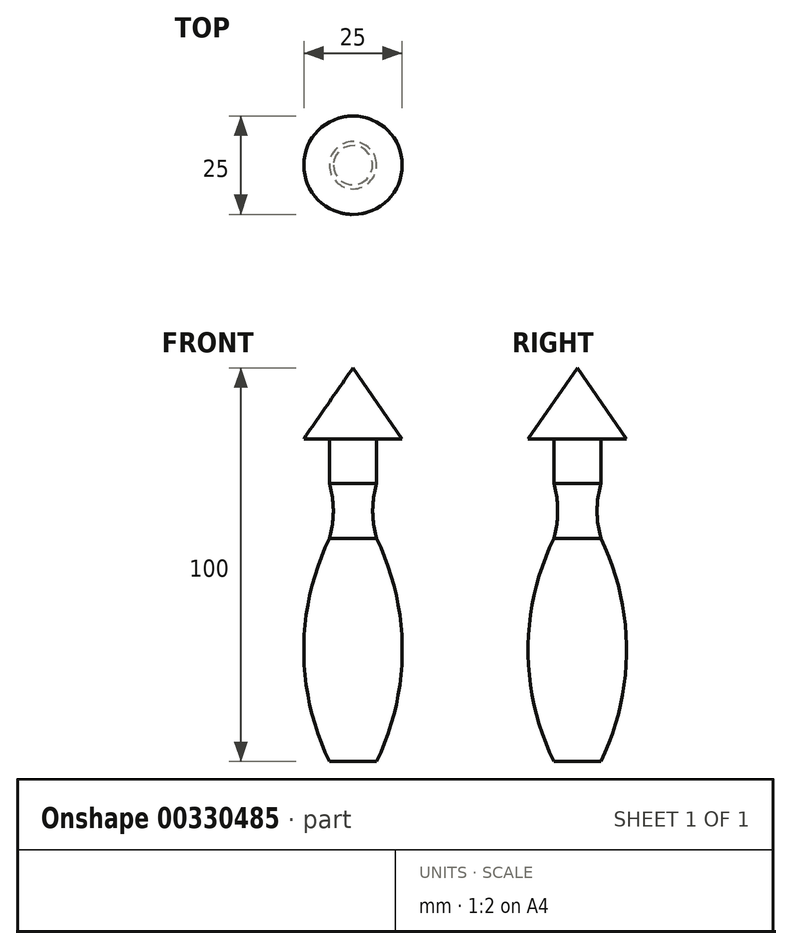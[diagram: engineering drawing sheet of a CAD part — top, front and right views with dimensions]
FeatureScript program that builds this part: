
annotation { "Feature Type Name" : "Feature", "Feature Type Description" : "" }
export const myFeature = defineFeature(function(context is Context, id is Id, definition is map)
    precondition{}
    {
        {
            var Q0;
            Q0=qCreatedBy(makeId("Front.planeOp"),FACE);
            var sketch = newSketch(context, id + "F0", { "sketchPlane" : qUnion([Q0])});
            skLineSegment(sketch, "E0", {"start": v(0, 0) * mm, "end": v(12.5, -18) * mm});
            skLineSegment(sketch, "E1", {"start": v(12.5, -18) * mm, "end": v(6, -18) * mm});
            skLineSegment(sketch, "E2", {"start": v(6, -18) * mm, "end": v(6, -29.33) * mm});
            skArc(sketch, "E3", {"start": v(6, -29.33) * mm, "mid": v(5, -36.33) * mm, "end": v(6, -43.33) * mm});
            skArc(sketch, "E4", {"start": v(6, -100) * mm, "mid": v(12.5, -71.67) * mm, "end": v(6, -43.33) * mm});
            skLineSegment(sketch, "E5", {"start": v(6, -100) * mm, "end": v(0, -100) * mm});
            skLineSegment(sketch, "E6", {"start": v(0, -100) * mm, "end": v(0, 0) * mm});
            skSolve(sketch);
        }
        {
            var Q0;
            Q0=makeQuery(id+"F0.imprint","IMPRINT",FACE,{"disambiguationData":[TD([[makeQuery(id+"F0.imprint","IMPRINT",EDGE,{"derivedFrom":sQuery(id+"F0.wireOp",EDGE,"E0")}),-1.0]])]});
            var Q1;
            Q1=sQuery(id+"F0.wireOp",EDGE,"E6");
            revolve(context, id + "F1", {"entities" : qUnion([Q0]), "axis" : qUnion([Q1]), "revolveType" : RevolveType.FULL});
        }
    });
